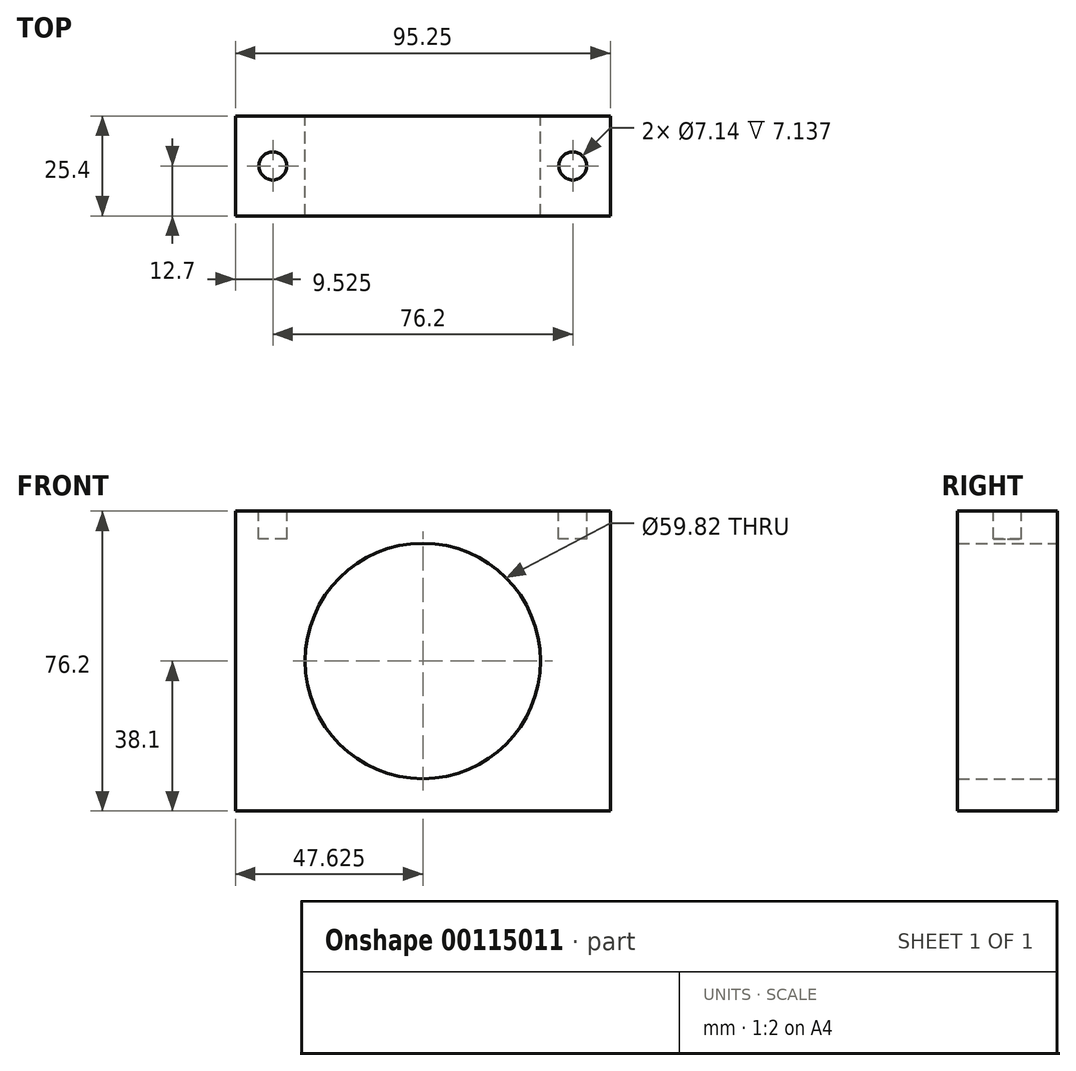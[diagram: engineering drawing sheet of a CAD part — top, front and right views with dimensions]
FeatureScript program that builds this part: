
annotation { "Feature Type Name" : "Feature", "Feature Type Description" : "" }
export const myFeature = defineFeature(function(context is Context, id is Id, definition is map)
    precondition{}
    {
        {
            var Q0;
            Q0=qCreatedBy(makeId("Front.planeOp"),FACE);
            var sketch = newSketch(context, id + "F0", { "sketchPlane" : qUnion([Q0])});
            skLineSegment(sketch, "E0.bottom", {"start": v(-95.25, 76.2) * mm, "end": v(0, 76.2) * mm});
            skLineSegment(sketch, "E0.top", {"start": v(-95.25, 0) * mm, "end": v(0, 0) * mm});
            skLineSegment(sketch, "E0.left", {"start": v(-95.25, 76.2) * mm, "end": v(-95.25, 0) * mm});
            skLineSegment(sketch, "E0.right", {"start": v(0, 76.2) * mm, "end": v(0, 0) * mm});
            skLineSegment(sketch, "E1", {"start": v(-47.62, 0) * mm, "end": v(-47.62, 76.2) * mm, "construction": true});
            skLineSegment(sketch, "E2", {"start": v(-95.25, 38.1) * mm, "end": v(0, 38.1) * mm, "construction": true});
            skCircle(sketch, "E3", {"center": v(-47.62, 38.1) * mm, "radius": 29.91 * mm});
            skSolve(sketch);
        }
        {
            var Q0;
            Q0=makeQuery(id+"F0.imprint","IMPRINT",FACE,{"disambiguationData":[TD([[makeQuery(id+"F0.imprint","IMPRINT",EDGE,{"derivedFrom":sQuery(id+"F0.wireOp",EDGE,"E0.bottom")}),-1.0]])]});
            extrude(context, id + "F1", {"entities" : qUnion([Q0]), "depth" : 25.4 * mm});
        }
        {
            var Q0;
            Q0=makeQuery(id+"F1.opExtrude","SWEPT_FACE",FACE,{"disambiguationData":[OSD([sQuery(id+"F0.wireOp",EDGE,"E0.bottom")])]});
            var sketch = newSketch(context, id + "F2", { "sketchPlane" : qUnion([Q0])});
            skLineSegment(sketch, "E4", {"start": v(-95.25, -12.7) * mm, "end": v(0, -12.7) * mm, "construction": true});
            skLineSegment(sketch, "E5", {"start": v(-47.63, 0) * mm, "end": v(-47.63, -25.4) * mm, "construction": true});
            skLineSegment(sketch, "E6", {"start": v(-85.73, 0) * mm, "end": v(-85.73, -25.4) * mm, "construction": true});
            skLineSegment(sketch, "E7", {"start": v(-9.53, 0) * mm, "end": v(-9.52, -25.4) * mm, "construction": true});
            skCircle(sketch, "E8", {"center": v(-85.73, -12.7) * mm, "radius": 3.57 * mm});
            skCircle(sketch, "E9", {"center": v(-9.52, -12.7) * mm, "radius": 3.57 * mm});
            skSolve(sketch);
        }
        {
            var Q0;
            Q0=makeQuery(id+"F2.imprint","IMPRINT",FACE,{"disambiguationData":[TD([[makeQuery(id+"F2.imprint","IMPRINT",EDGE,{"derivedFrom":sQuery(id+"F2.wireOp",EDGE,"E9")}),1.0]])]});
            var Q1;
            Q1=makeQuery(id+"F2.imprint","IMPRINT",FACE,{"disambiguationData":[TD([[makeQuery(id+"F2.imprint","IMPRINT",EDGE,{"derivedFrom":sQuery(id+"F2.wireOp",EDGE,"E8")}),1.0]])]});
            extrude(context, id + "F3", {"entities" : qUnion([Q0, Q1]), "operationType" : NewBodyOperationType.REMOVE, "oppositeDirection" : true, "depth" : 7.14 * mm});
        }
    });
